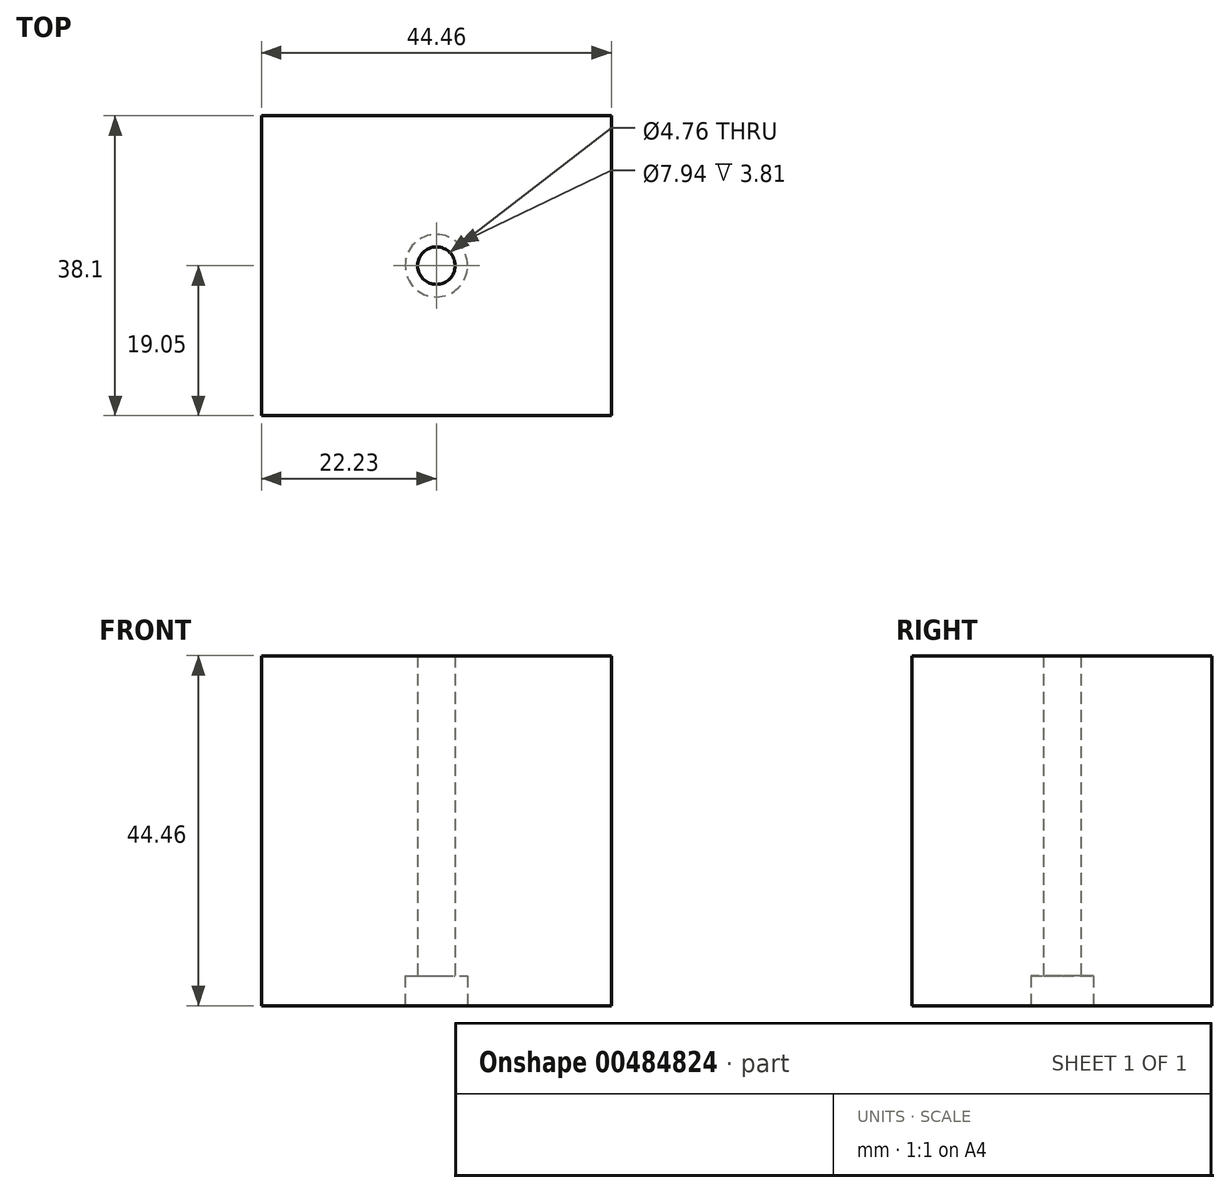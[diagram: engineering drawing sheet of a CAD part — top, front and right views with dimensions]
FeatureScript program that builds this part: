
annotation { "Feature Type Name" : "Feature", "Feature Type Description" : "" }
export const myFeature = defineFeature(function(context is Context, id is Id, definition is map)
    precondition{}
    {
        {
            var Q0;
            Q0=qCreatedBy(makeId("Front.planeOp"),FACE);
            var sketch = newSketch(context, id + "F0", { "sketchPlane" : qUnion([Q0])});
            skLineSegment(sketch, "E0.bottom", {"start": v(-22.22, 22.23) * mm, "end": v(22.23, 22.23) * mm});
            skLineSegment(sketch, "E0.top", {"start": v(-22.22, -22.23) * mm, "end": v(22.23, -22.23) * mm});
            skLineSegment(sketch, "E0.left", {"start": v(-22.22, 22.23) * mm, "end": v(-22.22, -22.23) * mm});
            skLineSegment(sketch, "E0.right", {"start": v(22.23, 22.23) * mm, "end": v(22.23, -22.23) * mm});
            skSolve(sketch);
        }
        {
            var Q0;
            Q0 = qSketchRegion(id + "F0", true);
            extrude(context, id + "F1", {"entities" : qUnion([Q0]), "depth" : 38.1 * mm, "symmetric" : true});
        }
        {
            var Q0;
            Q0=makeQuery(id+"F1.opExtrude","SWEPT_FACE",FACE,{"disambiguationData":[OSD([sQuery(id+"F0.wireOp",EDGE,"E0.top")])]});
            var sketch = newSketch(context, id + "F2", { "sketchPlane" : qUnion([Q0])});
            skCircle(sketch, "E1", {"center": v(0, 0) * mm, "radius": 3.97 * mm});
            skCircle(sketch, "E2", {"center": v(0, 0) * mm, "radius": 2.38 * mm});
            skSolve(sketch);
        }
        {
            var Q0;
            Q0=makeQuery(id+"F2.imprint","IMPRINT",FACE,{"disambiguationData":[TD([[makeQuery(id+"F2.imprint","IMPRINT",EDGE,{"derivedFrom":sQuery(id+"F2.wireOp",EDGE,"E2")}),1.0]])]});
            var Q1;
            Q1=sQuery(id+"F2.wireOp",EDGE,"E2");
            extrude(context, id + "F3", {"entities" : qUnion([Q0]), "operationType" : NewBodyOperationType.REMOVE, "surfaceEntities" : qUnion([Q1]), "endBound" : BoundingType.THROUGH_ALL, "oppositeDirection" : true, "depth" : 25.4 * mm});
        }
        {
            var Q0;
            Q0=makeQuery(id+"F2.imprint","IMPRINT",FACE,{"disambiguationData":[TD([[makeQuery(id+"F2.imprint","IMPRINT",EDGE,{"derivedFrom":sQuery(id+"F2.wireOp",EDGE,"E1")}),1.0]])]});
            extrude(context, id + "F4", {"entities" : qUnion([Q0]), "operationType" : NewBodyOperationType.REMOVE, "oppositeDirection" : true, "depth" : 3.8 * mm});
        }
    });
